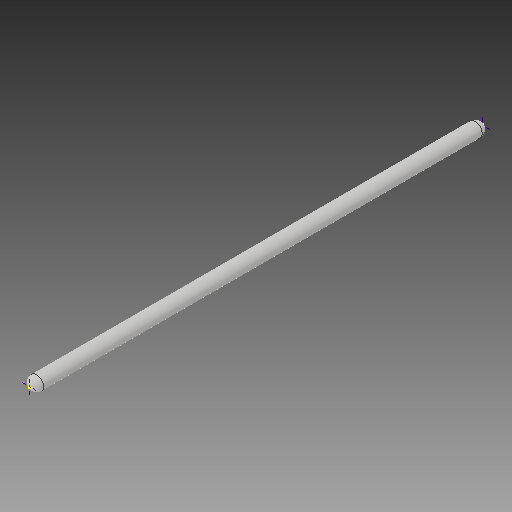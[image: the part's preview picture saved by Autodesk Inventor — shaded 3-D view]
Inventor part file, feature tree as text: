
AUTODESK INVENTOR PART (.ipt)
format: ipt  version: 2018 (Build 220112000, 112)  size: 81,920 bytes
history: native  units: mm
features: sketch x3, other x1, extrude x1, fillet x1
ambient origin geometry x8: Origin, YZ Plane, XZ Plane, XY Plane, X Axis, Y Axis, Z Axis, Center Point
bodies: Body1 (feature_tree)
feature tree (6):
  other  "ソリッド1"
  extrude  "押し出し1"  Depth=16.0mm
  sketch  "スケッチ2"
  sketch  "スケッチ3"
  fillet  "フィレット1"  Radius=516.0mm
  sketch  "スケッチ1"
